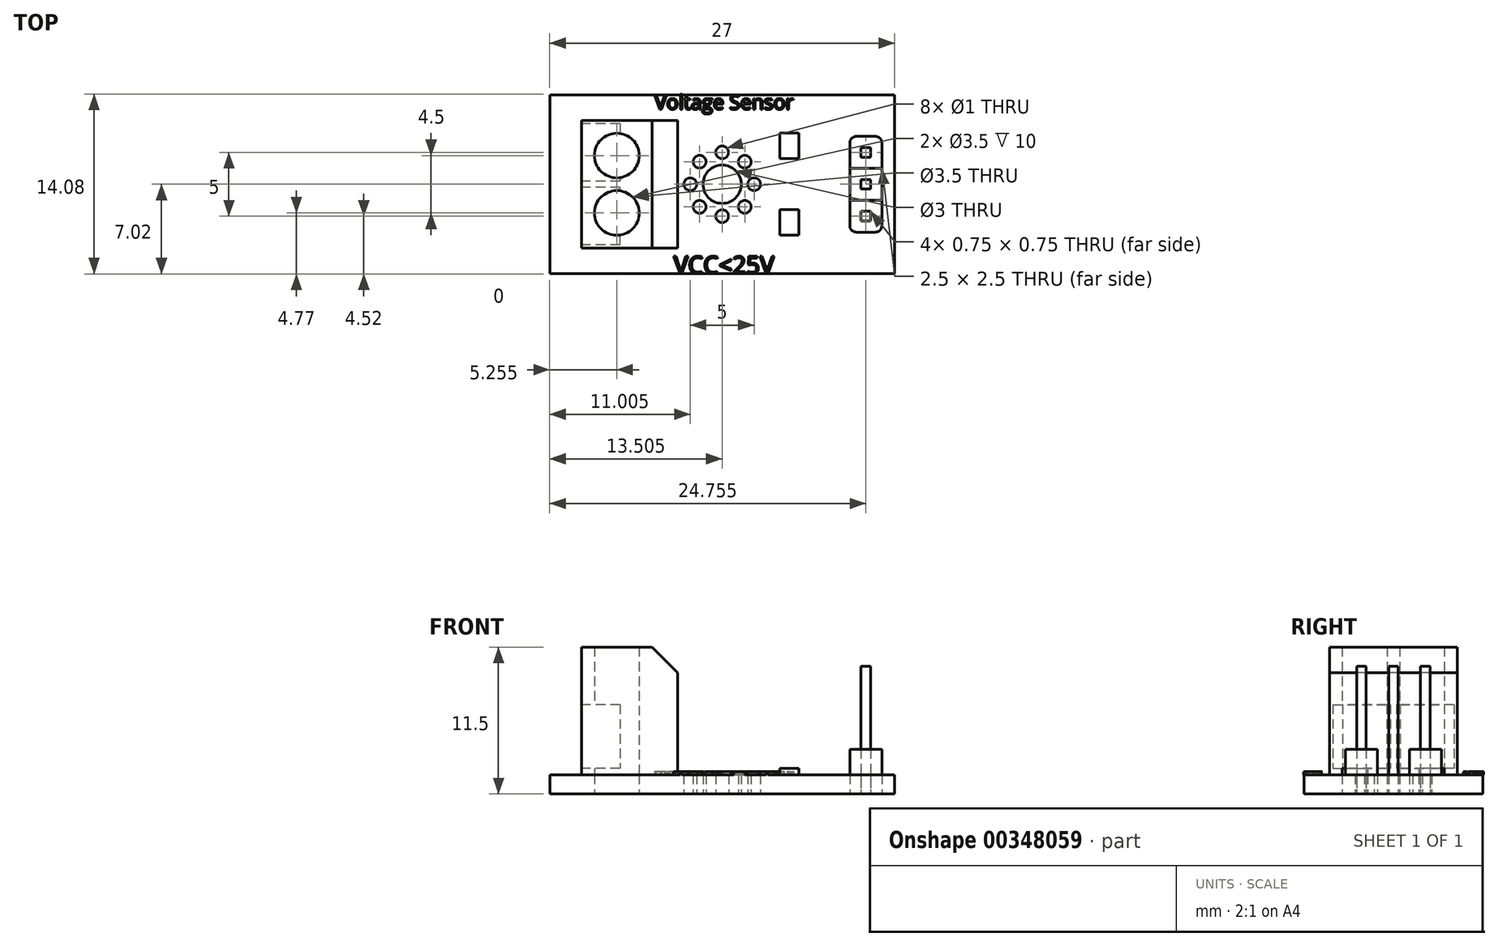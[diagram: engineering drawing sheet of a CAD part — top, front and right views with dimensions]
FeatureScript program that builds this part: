
annotation { "Feature Type Name" : "Feature", "Feature Type Description" : "" }
export const myFeature = defineFeature(function(context is Context, id is Id, definition is map)
    precondition{}
    {
        {
            var Q0;
            Q0=qCreatedBy(makeId("Top.planeOp"),FACE);
            var sketch = newSketch(context, id + "F0", { "sketchPlane" : qUnion([Q0])});
            skLineSegment(sketch, "E0.bottom", {"start": v(-13.7, 7) * mm, "end": v(13.3, 7) * mm});
            skLineSegment(sketch, "E0.top", {"start": v(-13.7, -7) * mm, "end": v(13.3, -7) * mm});
            skLineSegment(sketch, "E0.left", {"start": v(-13.7, 7) * mm, "end": v(-13.7, -7) * mm});
            skLineSegment(sketch, "E0.right", {"start": v(13.3, 7) * mm, "end": v(13.3, -7) * mm});
            skLineSegment(sketch, "E1.bottom", {"start": v(-11.2, 5) * mm, "end": v(-3.7, 5) * mm});
            skLineSegment(sketch, "E1.top", {"start": v(-11.2, -5) * mm, "end": v(-3.7, -5) * mm});
            skLineSegment(sketch, "E1.left", {"start": v(-11.2, 5) * mm, "end": v(-11.2, -5) * mm});
            skLineSegment(sketch, "E1.right", {"start": v(-3.7, 5) * mm, "end": v(-3.7, -5) * mm});
            skPoint(sketch, "E1.middle", {"position": v(-7.46, 0) * mm});
            skCircle(sketch, "E2", {"center": v(-0.2, 0) * mm, "radius": 1.5 * mm});
            skCircle(sketch, "E3", {"center": v(-0.2, 2.5) * mm, "radius": 0.5 * mm});
            skCircle(sketch, "E4.1.0", {"center": v(-1.97, 1.77) * mm, "radius": 0.5 * mm});
            skCircle(sketch, "E4.2.0", {"center": v(-2.7, 0) * mm, "radius": 0.5 * mm});
            skCircle(sketch, "E4.3.0", {"center": v(-1.97, -1.77) * mm, "radius": 0.5 * mm});
            skCircle(sketch, "E4.4.0", {"center": v(-0.2, -2.5) * mm, "radius": 0.5 * mm});
            skCircle(sketch, "E4.5.0", {"center": v(1.56, -1.77) * mm, "radius": 0.5 * mm});
            skCircle(sketch, "E4.6.0", {"center": v(2.3, 0) * mm, "radius": 0.5 * mm});
            skCircle(sketch, "E4.7.0", {"center": v(1.56, 1.77) * mm, "radius": 0.5 * mm});
            skPoint(sketch, "E5.middle", {"position": v(11.04, 0) * mm});
            skCircle(sketch, "E6", {"center": v(-8.46, 2.25) * mm, "radius": 1.75 * mm});
            skCircle(sketch, "E7.MirrorC", {"center": v(-8.46, -2.25) * mm, "radius": 1.75 * mm});
            skLineSegment(sketch, "E8.bottom", {"start": v(9.8, 3.75) * mm, "end": v(12.3, 3.75) * mm});
            skLineSegment(sketch, "E8.top", {"start": v(9.8, 1.25) * mm, "end": v(12.3, 1.25) * mm});
            skLineSegment(sketch, "E8.left", {"start": v(9.8, 3.75) * mm, "end": v(9.8, 1.25) * mm});
            skLineSegment(sketch, "E8.right", {"start": v(12.3, 3.75) * mm, "end": v(12.3, 1.25) * mm});
            skPoint(sketch, "E8.middle", {"position": v(11.04, 2.5) * mm});
            skLineSegment(sketch, "E9.MirrorCS", {"start": v(9.8, -1.25) * mm, "end": v(12.3, -1.25) * mm});
            skLineSegment(sketch, "E10.MirrorCS", {"start": v(9.8, -3.75) * mm, "end": v(9.8, -1.25) * mm});
            skLineSegment(sketch, "E11.MirrorCS", {"start": v(12.3, -3.75) * mm, "end": v(12.3, -1.25) * mm});
            skLineSegment(sketch, "E12.MirrorCS", {"start": v(9.8, -3.75) * mm, "end": v(12.3, -3.75) * mm});
            skLineSegment(sketch, "E13.left", {"start": v(9.8, 1.25) * mm, "end": v(9.8, -1.25) * mm});
            skLineSegment(sketch, "E13.right", {"start": v(12.3, 1.25) * mm, "end": v(12.3, -1.25) * mm});
            skLineSegment(sketch, "E14.bottom", {"start": v(10.67, 2.87) * mm, "end": v(11.42, 2.87) * mm});
            skLineSegment(sketch, "E14.top", {"start": v(10.67, 2.12) * mm, "end": v(11.42, 2.12) * mm});
            skLineSegment(sketch, "E14.left", {"start": v(10.67, 2.87) * mm, "end": v(10.67, 2.12) * mm});
            skLineSegment(sketch, "E14.right", {"start": v(11.42, 2.87) * mm, "end": v(11.42, 2.12) * mm});
            skLineSegment(sketch, "E15.MirrorCS", {"start": v(11.42, -2.87) * mm, "end": v(11.42, -2.12) * mm});
            skLineSegment(sketch, "E16.MirrorCS", {"start": v(10.67, -2.12) * mm, "end": v(11.42, -2.12) * mm});
            skLineSegment(sketch, "E17.MirrorCS", {"start": v(10.67, -2.87) * mm, "end": v(10.67, -2.12) * mm});
            skLineSegment(sketch, "E18.MirrorCS", {"start": v(10.67, -2.87) * mm, "end": v(11.42, -2.87) * mm});
            skLineSegment(sketch, "E19.bottom", {"start": v(10.67, 0.37) * mm, "end": v(11.42, 0.37) * mm});
            skLineSegment(sketch, "E19.top", {"start": v(10.67, -0.38) * mm, "end": v(11.42, -0.38) * mm});
            skLineSegment(sketch, "E19.left", {"start": v(10.67, 0.37) * mm, "end": v(10.67, -0.38) * mm});
            skLineSegment(sketch, "E19.right", {"start": v(11.42, 0.37) * mm, "end": v(11.42, -0.38) * mm});
            skSolve(sketch);
        }
        {
            var Q0;
            Q0=makeQuery(id+"F0.imprint","IMPRINT",FACE,{"disambiguationData":[TD([[makeQuery(id+"F0.imprint","IMPRINT",EDGE,{"derivedFrom":sQuery(id+"F0.wireOp",EDGE,"E0.bottom")}),-1.0]])]});
            var Q1;
            Q1=makeQuery(id+"F0.imprint","IMPRINT",FACE,{"disambiguationData":[TD([[makeQuery(id+"F0.imprint","IMPRINT",EDGE,{"derivedFrom":sQuery(id+"F0.wireOp",EDGE,"E1.bottom")}),-1.0]])]});
            var Q2;
            Q2=makeQuery(id+"F0.imprint","IMPRINT",FACE,{"disambiguationData":[TD([[makeQuery(id+"F0.imprint","IMPRINT",EDGE,{"derivedFrom":sQuery(id+"F0.wireOp",EDGE,"E5.bottom")}),-1.0]])]});
            var Q3;
            Q3=makeQuery(id+"F0.imprint","IMPRINT",FACE,{"disambiguationData":[TD([[makeQuery(id+"F0.imprint","IMPRINT",EDGE,{"derivedFrom":sQuery(id+"F0.wireOp",EDGE,"E6")}),1.0]])]});
            var Q4;
            Q4=makeQuery(id+"F0.imprint","IMPRINT",FACE,{"disambiguationData":[TD([[makeQuery(id+"F0.imprint","IMPRINT",EDGE,{"derivedFrom":sQuery(id+"F0.wireOp",EDGE,"E7.MirrorC")}),-1.0]])]});
            var Q5;
            Q5=makeQuery(id+"F0.imprint","IMPRINT",FACE,{"disambiguationData":[TD([[makeQuery(id+"F0.imprint","IMPRINT",EDGE,{"derivedFrom":sQuery(id+"F0.wireOp",EDGE,"tkM6wLA2-pvZo-Kndy-HpdZ-7V8mxi746QEr")}),-1.0]])]});
            var Q6;
            Q6=makeQuery(id+"F0.imprint","IMPRINT",FACE,{"disambiguationData":[TD([[makeQuery(id+"F0.imprint","IMPRINT",EDGE,{"derivedFrom":sQuery(id+"F0.wireOp",EDGE,"MCH4ug7d-YqV0-o7L3-g08O-QnCJyD3sXhG8")}),-1.0]])]});
            var Q7;
            Q7=makeQuery(id+"F0.imprint","IMPRINT",FACE,{"disambiguationData":[TD([[makeQuery(id+"F0.imprint","IMPRINT",EDGE,{"derivedFrom":sQuery(id+"F0.wireOp",EDGE,"05450763-7668-469e-ae58-0d2f795eb0030.MirrorC")}),1.0]])]});
            var Q8;
            Q8=makeQuery(id+"F0.imprint","IMPRINT",FACE,{"disambiguationData":[TD([[makeQuery(id+"F0.imprint","IMPRINT",EDGE,{"derivedFrom":sQuery(id+"F0.wireOp",EDGE,"E10.MirrorCS")}),-1.0]])]});
            var Q9;
            Q9=makeQuery(id+"F0.imprint","IMPRINT",FACE,{"disambiguationData":[TD([[makeQuery(id+"F0.imprint","IMPRINT",EDGE,{"derivedFrom":sQuery(id+"F0.wireOp",EDGE,"E8.bottom")}),-1.0]])]});
            var Q10;
            Q10=makeQuery(id+"F0.imprint","IMPRINT",FACE,{"disambiguationData":[TD([[makeQuery(id+"F0.imprint","IMPRINT",EDGE,{"derivedFrom":sQuery(id+"F0.wireOp",EDGE,"E8.top")}),-1.0]])]});
            extrude(context, id + "F1", {"entities" : qUnion([Q0, Q1, Q2, Q3, Q4, Q5, Q6, Q7, Q8, Q9, Q10]), "depth" : 1.5 * mm});
        }
        {
            var Q0;
            Q0=makeQuery(id+"F0.imprint","IMPRINT",FACE,{"disambiguationData":[TD([[makeQuery(id+"F0.imprint","IMPRINT",EDGE,{"derivedFrom":sQuery(id+"F0.wireOp",EDGE,"E1.bottom")}),-1.0]])]});
            extrude(context, id + "F2", {"entities" : qUnion([Q0]), "depth" : 11.5 * mm, "hasSecondDirection" : true, "secondDirectionOppositeDirection" : false, "secondDirectionDepth" : 1.5 * mm});
        }
        {
            var Q0;
            Q0=makeQuery(id+"F2.opExtrude","CAP_EDGE",EDGE,{"disambiguationData":[OSD([sQuery(id+"F0.wireOp",EDGE,"E1.right")])],"isStart":false});
            chamfer(context, id + "F3", {"entities" : qUnion([Q0]), "chamferType" : ChamferType.TWO_OFFSETS, "width1" : 2 * mm, "oppositeDirection" : false, "width2" : 2 * mm, "tangentPropagation" : true});
        }
        {
            var Q0;
            Q0=makeQuery(id+"F2.opExtrude","SWEPT_FACE",FACE,{"disambiguationData":[OSD([sQuery(id+"F0.wireOp",EDGE,"E1.left")])]});
            var sketch = newSketch(context, id + "F4", { "sketchPlane" : qUnion([Q0])});
            skLineSegment(sketch, "E20.bottom", {"start": v(-4.75, 7) * mm, "end": v(-0.25, 7) * mm});
            skLineSegment(sketch, "E20.top", {"start": v(-4.75, 2) * mm, "end": v(-0.25, 2) * mm});
            skLineSegment(sketch, "E20.left", {"start": v(-4.75, 7) * mm, "end": v(-4.75, 2) * mm});
            skLineSegment(sketch, "E20.right", {"start": v(-0.25, 7) * mm, "end": v(-0.25, 2) * mm});
            skLineSegment(sketch, "E21.MirrorCS", {"start": v(4.75, 7) * mm, "end": v(0.25, 7) * mm});
            skLineSegment(sketch, "E22.MirrorCS", {"start": v(0.25, 7) * mm, "end": v(0.25, 2) * mm});
            skLineSegment(sketch, "E23.MirrorCS", {"start": v(4.75, 2) * mm, "end": v(0.25, 2) * mm});
            skLineSegment(sketch, "E24.MirrorCS", {"start": v(4.75, 7) * mm, "end": v(4.75, 2) * mm});
            skSolve(sketch);
        }
        {
            var Q0;
            Q0=makeQuery(id+"F4.imprint","IMPRINT",FACE,{"disambiguationData":[TD([[makeQuery(id+"F4.imprint","IMPRINT",EDGE,{"derivedFrom":sQuery(id+"F4.wireOp",EDGE,"E20.bottom")}),-1.0]])]});
            var Q1;
            Q1=makeQuery(id+"F4.imprint","IMPRINT",FACE,{"disambiguationData":[TD([[makeQuery(id+"F4.imprint","IMPRINT",EDGE,{"derivedFrom":sQuery(id+"F4.wireOp",EDGE,"E21.MirrorCS")}),1.0]])]});
            extrude(context, id + "F5", {"entities" : qUnion([Q0, Q1]), "operationType" : NewBodyOperationType.REMOVE, "oppositeDirection" : true, "depth" : 3 * mm});
        }
        {
            var Q0;
            Q0=makeQuery(id+"F1.opExtrude","CAP_FACE",FACE,{"disambiguationData":[OSD([sQuery(id+"F0.wireOp",EDGE,"E0.bottom"),sQuery(id+"F0.wireOp",EDGE,"E0.top"),sQuery(id+"F0.wireOp",EDGE,"E0.left"),sQuery(id+"F0.wireOp",EDGE,"E0.right"),sQuery(id+"F0.wireOp",EDGE,"E2"),sQuery(id+"F0.wireOp",EDGE,"E3"),sQuery(id+"F0.wireOp",EDGE,"E4.1.0"),sQuery(id+"F0.wireOp",EDGE,"E4.2.0"),sQuery(id+"F0.wireOp",EDGE,"E4.3.0"),sQuery(id+"F0.wireOp",EDGE,"E4.4.0"),sQuery(id+"F0.wireOp",EDGE,"E4.5.0"),sQuery(id+"F0.wireOp",EDGE,"E4.6.0"),sQuery(id+"F0.wireOp",EDGE,"E4.7.0"),sQuery(id+"F0.wireOp",EDGE,"E6"),sQuery(id+"F0.wireOp",EDGE,"E7.MirrorC"),sQuery(id+"F0.wireOp",EDGE,"tkM6wLA2-pvZo-Kndy-HpdZ-7V8mxi746QEr"),sQuery(id+"F0.wireOp",EDGE,"MCH4ug7d-YqV0-o7L3-g08O-QnCJyD3sXhG8"),sQuery(id+"F0.wireOp",EDGE,"05450763-7668-469e-ae58-0d2f795eb0030.MirrorC")])],"isStart":false});
            var sketch = newSketch(context, id + "F6", { "sketchPlane" : qUnion([Q0])});
            skLineSegment(sketch, "E25.bottom", {"start": v(4.3, 4) * mm, "end": v(5.8, 4) * mm});
            skLineSegment(sketch, "E25.top", {"start": v(4.3, 2) * mm, "end": v(5.8, 2) * mm});
            skLineSegment(sketch, "E25.left", {"start": v(4.3, 4) * mm, "end": v(4.3, 2) * mm});
            skLineSegment(sketch, "E25.right", {"start": v(5.8, 4) * mm, "end": v(5.8, 2) * mm});
            skPoint(sketch, "E25.middle", {"position": v(5.04, 3) * mm});
            skLineSegment(sketch, "E26.MirrorCS", {"start": v(4.3, -2) * mm, "end": v(5.8, -2) * mm});
            skLineSegment(sketch, "E27.MirrorCS", {"start": v(5.8, -4) * mm, "end": v(5.8, -2) * mm});
            skLineSegment(sketch, "E28.MirrorCS", {"start": v(4.3, -4) * mm, "end": v(4.3, -2) * mm});
            skLineSegment(sketch, "E29.MirrorCS", {"start": v(4.3, -4) * mm, "end": v(5.8, -4) * mm});
            skSolve(sketch);
        }
        {
            var Q0;
            Q0=makeQuery(id+"F6.imprint","IMPRINT",FACE,{"disambiguationData":[TD([[makeQuery(id+"F6.imprint","IMPRINT",EDGE,{"derivedFrom":sQuery(id+"F6.wireOp",EDGE,"E25.bottom")}),-1.0]])]});
            var Q1;
            Q1=makeQuery(id+"F6.imprint","IMPRINT",FACE,{"disambiguationData":[TD([[makeQuery(id+"F6.imprint","IMPRINT",EDGE,{"derivedFrom":sQuery(id+"F6.wireOp",EDGE,"E26.MirrorCS")}),-1.0]])]});
            extrude(context, id + "F7", {"entities" : qUnion([Q0, Q1]), "depth" : .5 * mm});
        }
        {
            var Q0;
            Q0=makeQuery(id+"F1.opExtrude","CAP_FACE",FACE,{"disambiguationData":[OSD([sQuery(id+"F0.wireOp",EDGE,"E0.bottom"),sQuery(id+"F0.wireOp",EDGE,"E0.top"),sQuery(id+"F0.wireOp",EDGE,"E0.left"),sQuery(id+"F0.wireOp",EDGE,"E0.right"),sQuery(id+"F0.wireOp",EDGE,"E2"),sQuery(id+"F0.wireOp",EDGE,"E3"),sQuery(id+"F0.wireOp",EDGE,"E4.1.0"),sQuery(id+"F0.wireOp",EDGE,"E4.2.0"),sQuery(id+"F0.wireOp",EDGE,"E4.3.0"),sQuery(id+"F0.wireOp",EDGE,"E4.4.0"),sQuery(id+"F0.wireOp",EDGE,"E4.5.0"),sQuery(id+"F0.wireOp",EDGE,"E4.6.0"),sQuery(id+"F0.wireOp",EDGE,"E4.7.0"),sQuery(id+"F0.wireOp",EDGE,"E6"),sQuery(id+"F0.wireOp",EDGE,"E7.MirrorC"),sQuery(id+"F0.wireOp",EDGE,"tkM6wLA2-pvZo-Kndy-HpdZ-7V8mxi746QEr"),sQuery(id+"F0.wireOp",EDGE,"MCH4ug7d-YqV0-o7L3-g08O-QnCJyD3sXhG8"),sQuery(id+"F0.wireOp",EDGE,"05450763-7668-469e-ae58-0d2f795eb0030.MirrorC")])],"isStart":false});
            var sketch = newSketch(context, id + "F8", { "sketchPlane" : qUnion([Q0])});
            skText(sketch, "E30", { "text": "Voltage Sensor", "fontName": "OpenSans-Regular.ttf"});
            skText(sketch, "E31", { "text": "VCC<25V", "fontName": "OpenSans-Regular.ttf"});
            const initialGuessF8  = {"E30": [-0.0055, 0.00587, 1, 0, 0.00113], "E31": [-0.004, -0.007, 1, 0, 0.00136]};
            skSetInitialGuess(sketch, initialGuessF8);
            skSolve(sketch);
        }
        {
            var Q0;
            {var subQ0=sQuery(id+"F8.wireOp",EDGE,"E30.sketch_text.stroke-26");Q0=makeQuery(id+"F8.imprint","IMPRINT",FACE,{"disambiguationData":[TD([[makeQuery(id+"F8.imprint","IMPRINT",EDGE,{"derivedFrom":subQ0}),-1.0]])]});}
            var Q1;
            Q1=makeQuery(id+"F8.imprint","IMPRINT",FACE,{"disambiguationData":[TD([[makeQuery(id+"F8.imprint","IMPRINT",EDGE,{"derivedFrom":sQuery(id+"F8.wireOp",EDGE,"E30.sketch_text.stroke-9")}),-1.0]])]});
            var Q2;
            Q2=makeQuery(id+"F8.imprint","IMPRINT",FACE,{"disambiguationData":[TD([[makeQuery(id+"F8.imprint","IMPRINT",EDGE,{"derivedFrom":sQuery(id+"F8.wireOp",EDGE,"E30.sketch_text.stroke-242")}),-1.0]])]});
            var Q3;
            Q3=makeQuery(id+"F8.imprint","IMPRINT",FACE,{"disambiguationData":[TD([[makeQuery(id+"F8.imprint","IMPRINT",EDGE,{"derivedFrom":sQuery(id+"F8.wireOp",EDGE,"E30.sketch_text.stroke-183")}),-1.0]])]});
            var Q4;
            Q4=makeQuery(id+"F8.imprint","IMPRINT",FACE,{"disambiguationData":[TD([[makeQuery(id+"F8.imprint","IMPRINT",EDGE,{"derivedFrom":sQuery(id+"F8.wireOp",EDGE,"E30.sketch_text.stroke-30")}),-1.0]])]});
            var Q5;
            Q5=makeQuery(id+"F8.imprint","IMPRINT",FACE,{"disambiguationData":[TD([[makeQuery(id+"F8.imprint","IMPRINT",EDGE,{"derivedFrom":sQuery(id+"F8.wireOp",EDGE,"E30.sketch_text.stroke-0")}),-1.0]])]});
            var Q6;
            Q6=makeQuery(id+"F8.imprint","IMPRINT",FACE,{"disambiguationData":[TD([[makeQuery(id+"F8.imprint","IMPRINT",EDGE,{"derivedFrom":sQuery(id+"F8.wireOp",EDGE,"E30.sketch_text.stroke-139")}),-1.0]])]});
            var Q7;
            Q7=makeQuery(id+"F8.imprint","IMPRINT",FACE,{"disambiguationData":[TD([[makeQuery(id+"F8.imprint","IMPRINT",EDGE,{"derivedFrom":sQuery(id+"F8.wireOp",EDGE,"E30.sketch_text.stroke-120")}),-1.0]])]});
            var Q8;
            {var subQ0=sQuery(id+"F8.wireOp",EDGE,"E30.sketch_text.stroke-154");var subQ1=sQuery(id+"F8.wireOp",EDGE,"E30.sketch_text.stroke-153");var subQ2=makeQuery(id+"F8.imprint","INTERSECT",VERTEX,{"derivedFrom":[subQ1,subQ0]});Q8=makeQuery(id+"F8.imprint","IMPRINT",FACE,{"disambiguationData":[TD([[makeQuery(id+"F8.imprint","IMPRINT",EDGE,{"disambiguationData":[TD([[subQ2,1.0]])],"derivedFrom":subQ1}),-1.0]])]});}
            var Q9;
            {var subQ0=sQuery(id+"F8.wireOp",EDGE,"E30.sketch_text.stroke-28");Q9=makeQuery(id+"F8.imprint","IMPRINT",FACE,{"disambiguationData":[TD([[makeQuery(id+"F8.imprint","IMPRINT",EDGE,{"derivedFrom":subQ0}),-1.0]])]});}
            var Q10;
            Q10=makeQuery(id+"F8.imprint","IMPRINT",FACE,{"disambiguationData":[TD([[makeQuery(id+"F8.imprint","IMPRINT",EDGE,{"derivedFrom":sQuery(id+"F8.wireOp",EDGE,"E30.sketch_text.stroke-200")}),-1.0]])]});
            var Q11;
            Q11=makeQuery(id+"F8.imprint","IMPRINT",FACE,{"disambiguationData":[TD([[makeQuery(id+"F8.imprint","IMPRINT",EDGE,{"derivedFrom":sQuery(id+"F8.wireOp",EDGE,"E30.sketch_text.stroke-164")}),-1.0]])]});
            var Q12;
            Q12=makeQuery(id+"F8.imprint","IMPRINT",FACE,{"disambiguationData":[TD([[makeQuery(id+"F8.imprint","IMPRINT",EDGE,{"derivedFrom":sQuery(id+"F8.wireOp",EDGE,"E30.sketch_text.stroke-49")}),-1.0]])]});
            var Q13;
            Q13=makeQuery(id+"F8.imprint","IMPRINT",FACE,{"disambiguationData":[TD([[makeQuery(id+"F8.imprint","IMPRINT",EDGE,{"derivedFrom":sQuery(id+"F8.wireOp",EDGE,"E30.sketch_text.stroke-225")}),-1.0]])]});
            var Q14;
            Q14=makeQuery(id+"F8.imprint","IMPRINT",FACE,{"disambiguationData":[TD([[makeQuery(id+"F8.imprint","IMPRINT",EDGE,{"derivedFrom":sQuery(id+"F8.wireOp",EDGE,"E30.sketch_text.stroke-76")}),-1.0]])]});
            var Q15;
            Q15=makeQuery(id+"F8.imprint","IMPRINT",FACE,{"disambiguationData":[TD([[makeQuery(id+"F8.imprint","IMPRINT",EDGE,{"derivedFrom":sQuery(id+"F8.wireOp",EDGE,"E31.sketch_text.stroke-24")}),-1.0]])]});
            var Q16;
            Q16=makeQuery(id+"F8.imprint","IMPRINT",FACE,{"disambiguationData":[TD([[makeQuery(id+"F8.imprint","IMPRINT",EDGE,{"derivedFrom":sQuery(id+"F8.wireOp",EDGE,"E31.sketch_text.stroke-9")}),-1.0]])]});
            var Q17;
            Q17=makeQuery(id+"F8.imprint","IMPRINT",FACE,{"disambiguationData":[TD([[makeQuery(id+"F8.imprint","IMPRINT",EDGE,{"derivedFrom":sQuery(id+"F8.wireOp",EDGE,"E31.sketch_text.stroke-0")}),-1.0]])]});
            var Q18;
            Q18=makeQuery(id+"F8.imprint","IMPRINT",FACE,{"disambiguationData":[TD([[makeQuery(id+"F8.imprint","IMPRINT",EDGE,{"derivedFrom":sQuery(id+"F8.wireOp",EDGE,"E31.sketch_text.stroke-46")}),1.0]])]});
            var Q19;
            Q19=makeQuery(id+"F8.imprint","IMPRINT",FACE,{"disambiguationData":[TD([[makeQuery(id+"F8.imprint","IMPRINT",EDGE,{"derivedFrom":sQuery(id+"F8.wireOp",EDGE,"E31.sketch_text.stroke-39")}),-1.0]])]});
            var Q20;
            Q20=makeQuery(id+"F8.imprint","IMPRINT",FACE,{"disambiguationData":[TD([[makeQuery(id+"F8.imprint","IMPRINT",EDGE,{"derivedFrom":sQuery(id+"F8.wireOp",EDGE,"E31.sketch_text.stroke-85")}),-1.0]])]});
            var Q21;
            {var subQ0=sQuery(id+"F8.wireOp",EDGE,"E31.sketch_text.stroke-70");var subQ1=sQuery(id+"F8.wireOp",EDGE,"E31.sketch_text.stroke-69");var subQ2=makeQuery(id+"F8.imprint","INTERSECT",VERTEX,{"derivedFrom":[subQ1,subQ0]});Q21=makeQuery(id+"F8.imprint","IMPRINT",FACE,{"disambiguationData":[TD([[makeQuery(id+"F8.imprint","IMPRINT",EDGE,{"disambiguationData":[TD([[subQ2,1.0]])],"derivedFrom":subQ1}),-1.0]])]});}
            var Q22;
            {var subQ0=sQuery(id+"F8.wireOp",EDGE,"E31.sketch_text.stroke-16");var subQ1=sQuery(id+"F8.wireOp",EDGE,"E31.sketch_text.stroke-15");var subQ2=makeQuery(id+"F8.imprint","INTERSECT",VERTEX,{"derivedFrom":[subQ1,subQ0]});Q22=makeQuery(id+"F8.imprint","IMPRINT",FACE,{"disambiguationData":[TD([[makeQuery(id+"F8.imprint","IMPRINT",EDGE,{"disambiguationData":[TD([[subQ2,1.0]])],"derivedFrom":subQ1}),-1.0]])]});}
            var Q23;
            {var subQ0=sQuery(id+"F8.wireOp",EDGE,"E31.sketch_text.stroke-31");var subQ1=sQuery(id+"F8.wireOp",EDGE,"E31.sketch_text.stroke-30");var subQ2=makeQuery(id+"F8.imprint","INTERSECT",VERTEX,{"derivedFrom":[subQ1,subQ0]});Q23=makeQuery(id+"F8.imprint","IMPRINT",FACE,{"disambiguationData":[TD([[makeQuery(id+"F8.imprint","IMPRINT",EDGE,{"disambiguationData":[TD([[subQ2,1.0]])],"derivedFrom":subQ1}),-1.0]])]});}
            var Q24;
            Q24=makeQuery(id+"F8.imprint","IMPRINT",FACE,{"disambiguationData":[TD([[makeQuery(id+"F8.imprint","IMPRINT",EDGE,{"derivedFrom":sQuery(id+"F8.wireOp",EDGE,"E31.sketch_text.stroke-66")}),-1.0]])]});
            extrude(context, id + "F9", {"entities" : qUnion([Q0, Q1, Q2, Q3, Q4, Q5, Q6, Q7, Q8, Q9, Q10, Q11, Q12, Q13, Q14, Q15, Q16, Q17, Q18, Q19, Q20, Q21, Q22, Q23, Q24]), "operationType" : NewBodyOperationType.ADD, "depth" : .25 * mm});
        }
        {
            var Q0;
            Q0=makeQuery(id+"F0.imprint","IMPRINT",FACE,{"disambiguationData":[TD([[makeQuery(id+"F0.imprint","IMPRINT",EDGE,{"derivedFrom":sQuery(id+"F0.wireOp",EDGE,"05450763-7668-469e-ae58-0d2f795eb0030.MirrorC")}),1.0]])]});
            var Q1;
            Q1=makeQuery(id+"F0.imprint","IMPRINT",FACE,{"disambiguationData":[TD([[makeQuery(id+"F0.imprint","IMPRINT",EDGE,{"derivedFrom":sQuery(id+"F0.wireOp",EDGE,"tkM6wLA2-pvZo-Kndy-HpdZ-7V8mxi746QEr")}),-1.0]])]});
            var Q2;
            Q2=makeQuery(id+"F0.imprint","IMPRINT",FACE,{"disambiguationData":[TD([[makeQuery(id+"F0.imprint","IMPRINT",EDGE,{"derivedFrom":sQuery(id+"F0.wireOp",EDGE,"MCH4ug7d-YqV0-o7L3-g08O-QnCJyD3sXhG8")}),-1.0]])]});
            var Q3;
            Q3=makeQuery(id+"F0.imprint","IMPRINT",FACE,{"disambiguationData":[TD([[makeQuery(id+"F0.imprint","IMPRINT",EDGE,{"derivedFrom":sQuery(id+"F0.wireOp",EDGE,"E8.bottom")}),-1.0]])]});
            var Q4;
            Q4=makeQuery(id+"F0.imprint","IMPRINT",FACE,{"disambiguationData":[TD([[makeQuery(id+"F0.imprint","IMPRINT",EDGE,{"derivedFrom":sQuery(id+"F0.wireOp",EDGE,"E10.MirrorCS")}),-1.0]])]});
            var Q5;
            Q5=makeQuery(id+"F0.imprint","IMPRINT",FACE,{"disambiguationData":[TD([[makeQuery(id+"F0.imprint","IMPRINT",EDGE,{"derivedFrom":sQuery(id+"F0.wireOp",EDGE,"E8.top")}),-1.0]])]});
            extrude(context, id + "F10", {"entities" : qUnion([Q0, Q1, Q2, Q3, Q4, Q5]), "depth" : 3.5 * mm, "hasSecondDirection" : true, "secondDirectionOppositeDirection" : false, "secondDirectionDepth" : 1.5 * mm});
        }
        {
            var Q0;
            Q0=makeQuery(id+"F10.opExtrude","SWEPT_EDGE",EDGE,{"disambiguationData":[OSD([sQuery(id+"F0.wireOp",EDGE,"E11.MirrorCS"),sQuery(id+"F0.wireOp",EDGE,"E12.MirrorCS")])]});
            var Q1;
            Q1=makeQuery(id+"F10.opExtrude","SWEPT_EDGE",EDGE,{"disambiguationData":[OSD([sQuery(id+"F0.wireOp",EDGE,"E10.MirrorCS"),sQuery(id+"F0.wireOp",EDGE,"E12.MirrorCS")])]});
            var Q2;
            Q2=makeQuery(id+"F10.opExtrude","SWEPT_EDGE",EDGE,{"disambiguationData":[OSD([sQuery(id+"F0.wireOp",EDGE,"E8.bottom"),sQuery(id+"F0.wireOp",EDGE,"E8.left")])]});
            var Q3;
            Q3=makeQuery(id+"F10.opExtrude","SWEPT_EDGE",EDGE,{"disambiguationData":[OSD([sQuery(id+"F0.wireOp",EDGE,"E8.bottom"),sQuery(id+"F0.wireOp",EDGE,"E8.right")])]});
            fillet(context, id + "F11", {"entities" : qUnion([Q0, Q1, Q2, Q3]), "radius" : .5 * mm, "tangentPropagation" : true, "allowEdgeOverflow" : false});
        }
        {
            var Q0;
            Q0=makeQuery(id+"F0.imprint","IMPRINT",FACE,{"disambiguationData":[TD([[makeQuery(id+"F0.imprint","IMPRINT",EDGE,{"derivedFrom":sQuery(id+"F0.wireOp",EDGE,"E14.bottom")}),-1.0]])]});
            var Q1;
            Q1=makeQuery(id+"F0.imprint","IMPRINT",FACE,{"disambiguationData":[TD([[makeQuery(id+"F0.imprint","IMPRINT",EDGE,{"derivedFrom":sQuery(id+"F0.wireOp",EDGE,"E19.bottom")}),-1.0]])]});
            var Q2;
            Q2=makeQuery(id+"F0.imprint","IMPRINT",FACE,{"disambiguationData":[TD([[makeQuery(id+"F0.imprint","IMPRINT",EDGE,{"derivedFrom":sQuery(id+"F0.wireOp",EDGE,"E15.MirrorCS")}),1.0]])]});
            extrude(context, id + "F12", {"entities" : qUnion([Q0, Q1, Q2]), "depth" : 10 * mm});
        }
    });
